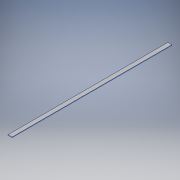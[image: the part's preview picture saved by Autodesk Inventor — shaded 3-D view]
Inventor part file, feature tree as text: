
AUTODESK INVENTOR PART (.ipt)
format: ipt  version: 2019 (Build 230136000, 136)  size: 95,232 bytes
history: native  units: in
note: dims shown in document units (in); Inventor stores cm internally (conversion verified against a paired STEP export)
features: extrude x1, sketch x1
ambient origin geometry x8: Origin, YZ Plane, XZ Plane, XY Plane, X Axis, Y Axis, Z Axis, Center Point
bodies: Solid1 (feature_tree)
feature tree (2):
  extrude  "Extrusion1"  Depth=0.5in
  sketch  "Sketch1"  dims[d0=19.685in d2=0.5in d3=0.063in d4=0.0in]
